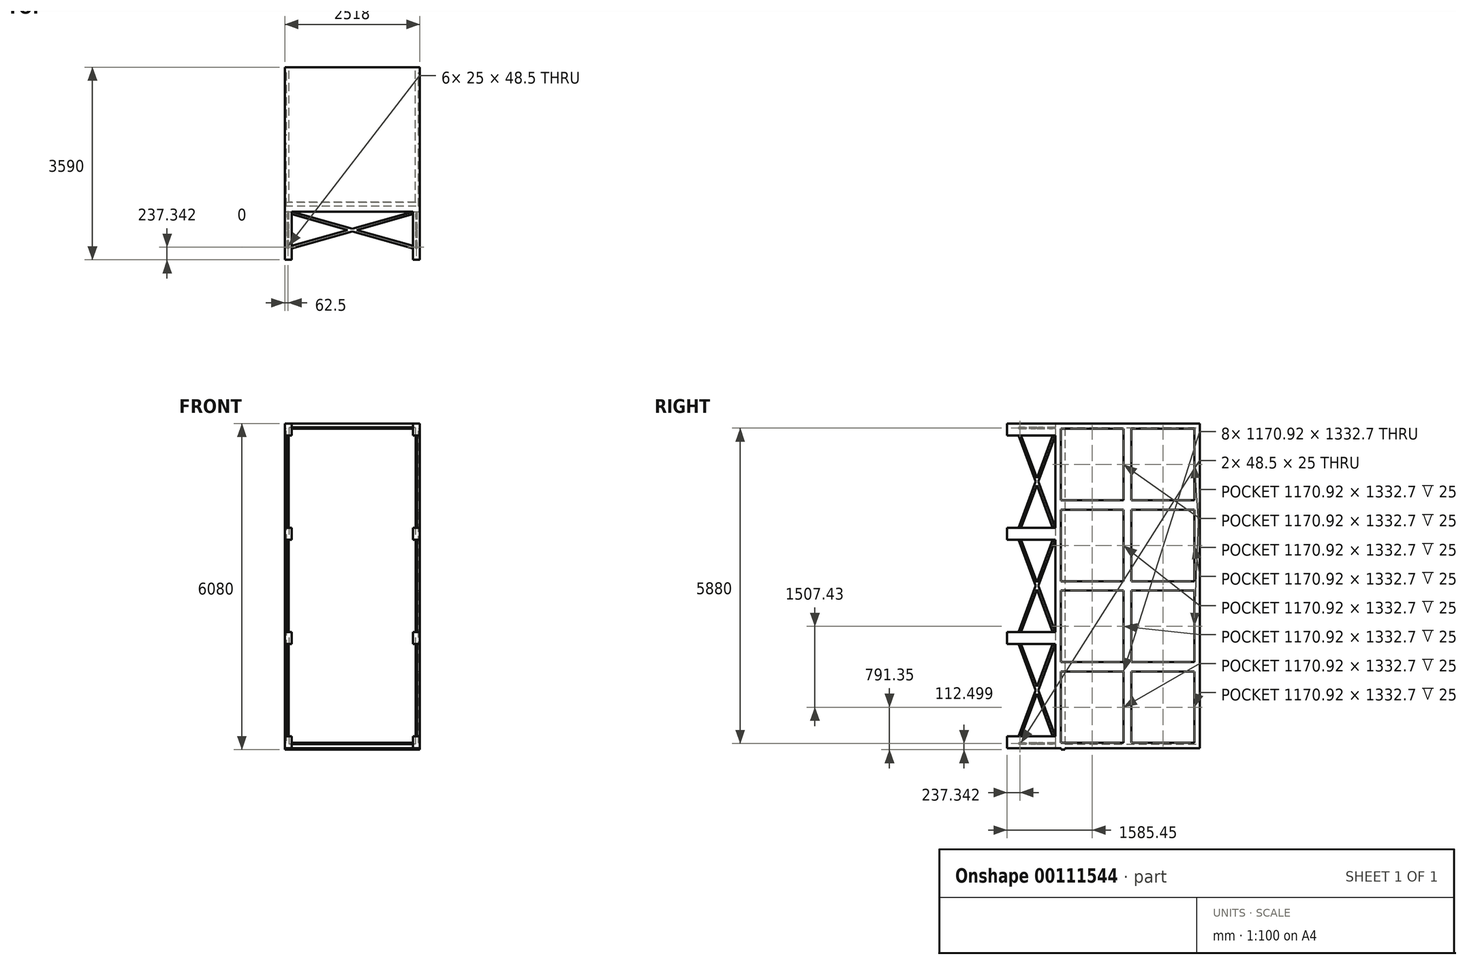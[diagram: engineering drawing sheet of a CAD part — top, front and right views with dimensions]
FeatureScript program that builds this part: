
annotation { "Feature Type Name" : "Feature", "Feature Type Description" : "" }
export const myFeature = defineFeature(function(context is Context, id is Id, definition is map)
    precondition{}
    {
        {
            var Q0;
            Q0=qCreatedBy(makeId("Right.planeOp"),FACE);
            var sketch = newSketch(context, id + "F0", { "sketchPlane" : qUnion([Q0])});
            skLineSegment(sketch, "E0.bottom", {"start": v(4722.94, 3226.74) * mm, "end": v(8312.94, 3226.74) * mm});
            skLineSegment(sketch, "E0.top", {"start": v(4722.94, -2828.26) * mm, "end": v(8312.94, -2828.26) * mm});
            skLineSegment(sketch, "E0.left", {"start": v(4722.94, 3226.74) * mm, "end": v(4722.94, -2828.26) * mm});
            skLineSegment(sketch, "E0.right", {"start": v(8312.94, 3226.74) * mm, "end": v(8312.94, -2828.26) * mm});
            skSolve(sketch);
        }
        {
            var Q0;
            Q0=qSketchRegion(id+"F0",true);
            extrude(context, id + "F1", {"entities" : qUnion([Q0]), "depth" : 2518 * mm});
        }
        {
            var Q0;
            Q0=makeQuery(id+"F1.opExtrude","SWEPT_FACE",FACE,{"disambiguationData":[OSD([sQuery(id+"F0.wireOp",EDGE,"E0.top")])]});
            var sketch = newSketch(context, id + "F2", { "sketchPlane" : qUnion([Q0])});
            skLineSegment(sketch, "E1.bottom", {"start": v(0, -5728.24) * mm, "end": v(2518, -5728.24) * mm});
            skLineSegment(sketch, "E1.top", {"start": v(0, -5798.24) * mm, "end": v(2518, -5798.24) * mm});
            skLineSegment(sketch, "E1.left", {"start": v(0, -5728.24) * mm, "end": v(0, -5798.24) * mm});
            skLineSegment(sketch, "E1.right", {"start": v(2518, -5728.24) * mm, "end": v(2518, -5798.24) * mm});
            skSolve(sketch);
        }
        {
            var Q0;
            Q0=qSketchRegion(id+"F2",true);
            extrude(context, id + "F3", {"entities" : qUnion([Q0]), "operationType" : NewBodyOperationType.ADD, "depth" : 25 * mm});
        }
        {
            var Q0;
            Q0=makeQuery(id+"F1.opExtrude","SWEPT_FACE",FACE,{"disambiguationData":[OSD([sQuery(id+"F0.wireOp",EDGE,"E0.right")])]});
            var sketch = newSketch(context, id + "F4", { "sketchPlane" : qUnion([Q0])});
            skLineSegment(sketch, "E2.0", {"start": v(-2438, 3146.74) * mm, "end": v(-80, 3146.74) * mm});
            skLineSegment(sketch, "E2.1", {"start": v(-2438, 3146.74) * mm, "end": v(-2438, -2748.26) * mm});
            skLineSegment(sketch, "E2.2", {"start": v(-2438, -2748.26) * mm, "end": v(-80, -2748.26) * mm});
            skLineSegment(sketch, "E2.3", {"start": v(-80, 3146.74) * mm, "end": v(-80, -2748.26) * mm});
            skSolve(sketch);
        }
        {
            var Q0;
            Q0=qSketchRegion(id+"F4",true);
            var Q1;
            Q1=makeQuery(id+"F3.opExtrude","SWEPT_FACE",FACE,{"disambiguationData":[OSD([sQuery(id+"F2.wireOp",EDGE,"E1.top")])]});
            extrude(context, id + "F5", {"entities" : qUnion([Q0]), "operationType" : NewBodyOperationType.REMOVE, "endBound" : BoundingType.UP_TO_SURFACE, "oppositeDirection" : true, "endBoundEntityFace" : qUnion([Q1]), "depth" : 25 * mm});
        }
        {
            var Q0;
            Q0=makeQuery(id+"F1.opExtrude","SWEPT_FACE",FACE,{"disambiguationData":[OSD([sQuery(id+"F0.wireOp",EDGE,"E0.left")])]});
            var sketch = newSketch(context, id + "F6", { "sketchPlane" : qUnion([Q0])});
            skLineSegment(sketch, "E3.bottom", {"start": v(0, 3226.74) * mm, "end": v(127, 3226.74) * mm});
            skLineSegment(sketch, "E3.top", {"start": v(0, 3005.36) * mm, "end": v(127, 3005.36) * mm});
            skLineSegment(sketch, "E3.left", {"start": v(0, 3226.74) * mm, "end": v(0, 3005.36) * mm});
            skLineSegment(sketch, "E3.right", {"start": v(127, 3226.74) * mm, "end": v(127, 3005.36) * mm});
            skLineSegment(sketch, "E4.0.1.0", {"start": v(0, 1282.2) * mm, "end": v(127, 1282.2) * mm});
            skLineSegment(sketch, "E4.0.1.1", {"start": v(0, 1282.2) * mm, "end": v(0, 1060.82) * mm});
            skLineSegment(sketch, "E4.0.1.2", {"start": v(127, 1282.2) * mm, "end": v(127, 1060.82) * mm});
            skLineSegment(sketch, "E4.0.1.3", {"start": v(0, 1060.82) * mm, "end": v(127, 1060.82) * mm});
            skLineSegment(sketch, "E4.0.2.0", {"start": v(0, -662.34) * mm, "end": v(127, -662.34) * mm});
            skLineSegment(sketch, "E4.0.2.1", {"start": v(0, -662.34) * mm, "end": v(0, -883.72) * mm});
            skLineSegment(sketch, "E4.0.2.2", {"start": v(127, -662.34) * mm, "end": v(127, -883.72) * mm});
            skLineSegment(sketch, "E4.0.2.3", {"start": v(0, -883.72) * mm, "end": v(127, -883.72) * mm});
            skLineSegment(sketch, "E4.0.3.0", {"start": v(0, -2606.89) * mm, "end": v(127, -2606.89) * mm});
            skLineSegment(sketch, "E4.0.3.1", {"start": v(0, -2606.89) * mm, "end": v(0, -2828.26) * mm});
            skLineSegment(sketch, "E4.0.3.2", {"start": v(127, -2606.89) * mm, "end": v(127, -2828.26) * mm});
            skLineSegment(sketch, "E4.0.3.3", {"start": v(0, -2828.26) * mm, "end": v(127, -2828.26) * mm});
            skLineSegment(sketch, "E4.1.0.0", {"start": v(2391, 3226.74) * mm, "end": v(2518, 3226.74) * mm});
            skLineSegment(sketch, "E4.1.0.1", {"start": v(2391, 3226.74) * mm, "end": v(2391, 3005.36) * mm});
            skLineSegment(sketch, "E4.1.0.2", {"start": v(2518, 3226.74) * mm, "end": v(2518, 3005.36) * mm});
            skLineSegment(sketch, "E4.1.0.3", {"start": v(2391, 3005.36) * mm, "end": v(2518, 3005.36) * mm});
            skLineSegment(sketch, "E4.1.1.0", {"start": v(2391, 1282.2) * mm, "end": v(2518, 1282.2) * mm});
            skLineSegment(sketch, "E4.1.1.1", {"start": v(2391, 1282.2) * mm, "end": v(2391, 1060.82) * mm});
            skLineSegment(sketch, "E4.1.1.2", {"start": v(2518, 1282.2) * mm, "end": v(2518, 1060.82) * mm});
            skLineSegment(sketch, "E4.1.1.3", {"start": v(2391, 1060.82) * mm, "end": v(2518, 1060.82) * mm});
            skLineSegment(sketch, "E4.1.2.0", {"start": v(2391, -662.34) * mm, "end": v(2518, -662.34) * mm});
            skLineSegment(sketch, "E4.1.2.1", {"start": v(2391, -662.34) * mm, "end": v(2391, -883.72) * mm});
            skLineSegment(sketch, "E4.1.2.2", {"start": v(2518, -662.34) * mm, "end": v(2518, -883.72) * mm});
            skLineSegment(sketch, "E4.1.2.3", {"start": v(2391, -883.72) * mm, "end": v(2518, -883.72) * mm});
            skLineSegment(sketch, "E4.1.3.0", {"start": v(2391, -2606.89) * mm, "end": v(2518, -2606.89) * mm});
            skLineSegment(sketch, "E4.1.3.1", {"start": v(2391, -2606.89) * mm, "end": v(2391, -2828.26) * mm});
            skLineSegment(sketch, "E4.1.3.2", {"start": v(2518, -2606.89) * mm, "end": v(2518, -2828.26) * mm});
            skLineSegment(sketch, "E4.1.3.3", {"start": v(2391, -2828.26) * mm, "end": v(2518, -2828.26) * mm});
            skLineSegment(sketch, "E4.direction1", {"start": v(0, 3226.74) * mm, "end": v(2391, 3226.74) * mm, "construction": true});
            skLineSegment(sketch, "E4.direction2", {"start": v(0, 3226.74) * mm, "end": v(0, 1282.2) * mm, "construction": true});
            skLineSegment(sketch, "E5.2", {"start": v(2518, 3226.74) * mm, "end": v(2518, -2828.26) * mm});
            skLineSegment(sketch, "E5.3", {"start": v(0, 3226.74) * mm, "end": v(0, -2828.26) * mm});
            skLineSegment(sketch, "E5.4", {"start": v(2518, -2828.26) * mm, "end": v(0, -2828.26) * mm});
            skSolve(sketch);
        }
        {
            var Q0;
            {var subQ15=sQuery(id+"F6.wireOp",EDGE,"E3.top");Q0=makeQuery(id+"F6.imprint","IMPRINT",FACE,{"disambiguationData":[TD([[makeQuery(id+"F6.imprint","IMPRINT",EDGE,{"derivedFrom":subQ15}),-1.0]])]});}
            extrude(context, id + "F7", {"entities" : qUnion([Q0]), "operationType" : NewBodyOperationType.REMOVE, "oppositeDirection" : true, "depth" : 900 * mm});
        }
        {
            var Q0;
            Q0=makeQuery(id+"F3.boolean.opBoolean","MERGE",FACE,{"derivedFrom":[makeQuery(id+"F1.opExtrude","CAP_FACE",FACE,{"disambiguationData":[OSD([sQuery(id+"F0.wireOp",EDGE,"E0.bottom"),sQuery(id+"F0.wireOp",EDGE,"E0.top"),sQuery(id+"F0.wireOp",EDGE,"E0.left"),sQuery(id+"F0.wireOp",EDGE,"E0.right")])],"isStart":true}),makeQuery(id+"F3.opExtrude","SWEPT_FACE",FACE,{"disambiguationData":[OSD([sQuery(id+"F2.wireOp",EDGE,"E1.left")])]})]});
            var sketch = newSketch(context, id + "F8", { "sketchPlane" : qUnion([Q0])});
            skLineSegment(sketch, "E6", {"start": v(-5622.94, -2606.89) * mm, "end": v(-5303.73, -1745.3) * mm});
            skLineSegment(sketch, "E7", {"start": v(-4984.53, -883.72) * mm, "end": v(-4936.03, -883.72) * mm});
            skLineSegment(sketch, "E8", {"start": v(-4936.03, -883.72) * mm, "end": v(-5255.24, -1745.3) * mm});
            skLineSegment(sketch, "E9", {"start": v(-5622.94, -1745.3) * mm, "end": v(-4658.41, -1745.3) * mm, "construction": true});
            skLineSegment(sketch, "E10.MirrorCS", {"start": v(-5622.94, -883.72) * mm, "end": v(-5303.73, -1745.3) * mm});
            skLineSegment(sketch, "E11.MirrorCS", {"start": v(-4936.03, -2606.89) * mm, "end": v(-5255.24, -1745.3) * mm});
            skLineSegment(sketch, "E12.0.1.0", {"start": v(-5622.94, -662.34) * mm, "end": v(-4984.53, 1060.82) * mm});
            skLineSegment(sketch, "E12.0.1.1", {"start": v(-4936.03, 1060.82) * mm, "end": v(-5574.44, -662.34) * mm});
            skLineSegment(sketch, "E12.0.1.2", {"start": v(-5622.94, 1060.82) * mm, "end": v(-4984.53, -662.34) * mm});
            skLineSegment(sketch, "E12.0.1.3", {"start": v(-4936.03, -662.34) * mm, "end": v(-5574.44, 1060.82) * mm});
            skLineSegment(sketch, "E12.0.2.0", {"start": v(-5622.94, 1282.2) * mm, "end": v(-4984.53, 3005.36) * mm});
            skLineSegment(sketch, "E12.0.2.1", {"start": v(-4936.03, 3005.36) * mm, "end": v(-5574.44, 1282.2) * mm});
            skLineSegment(sketch, "E12.0.2.2", {"start": v(-5622.94, 3005.36) * mm, "end": v(-4984.53, 1282.2) * mm});
            skLineSegment(sketch, "E12.0.2.3", {"start": v(-4936.03, 1282.2) * mm, "end": v(-5574.44, 3005.36) * mm});
            skLineSegment(sketch, "E12.direction1", {"start": v(-5622.94, -2606.89) * mm, "end": v(-5597.94, -2606.89) * mm, "construction": true});
            skLineSegment(sketch, "E12.direction2", {"start": v(-5622.94, -2606.89) * mm, "end": v(-5622.94, -662.34) * mm, "construction": true});
            skLineSegment(sketch, "E13.trimOffspring", {"start": v(-5279.48, -1810.75) * mm, "end": v(-5574.44, -2606.89) * mm});
            skLineSegment(sketch, "E14.trimOffspring", {"start": v(-5279.48, -1810.75) * mm, "end": v(-4984.53, -2606.89) * mm});
            skLineSegment(sketch, "E15.trimOffspring", {"start": v(-5279.48, -1679.85) * mm, "end": v(-4984.53, -883.72) * mm});
            skLineSegment(sketch, "E16.trimOffspring", {"start": v(-5279.48, -1679.85) * mm, "end": v(-5574.44, -883.72) * mm});
            skSolve(sketch);
        }
        {
            var Q0;
            Q0=qSketchRegion(id+"F8",true);
            var Q1;
            {var subQ5=sQuery(id+"F8.wireOp",EDGE,"E12.0.1.0");var subQ7=sQuery(id+"F8.wireOp",EDGE,"E12.0.1.2");var subQ9=makeQuery(id+"F8.imprint","INTERSECT",VERTEX,{"derivedFrom":[subQ5,subQ7]});Q1=makeQuery(id+"F8.imprint","IMPRINT",FACE,{"disambiguationData":[TD([[makeQuery(id+"F8.imprint","IMPRINT",EDGE,{"disambiguationData":[TD([[subQ9,-1.0]])],"derivedFrom":subQ7}),-1.0]])]});}
            var Q2;
            {var subQ1=sQuery(id+"F8.wireOp",EDGE,"E12.0.1.3");var subQ5=sQuery(id+"F8.wireOp",EDGE,"E12.0.1.1");var subQ6=makeQuery(id+"F8.imprint","INTERSECT",VERTEX,{"derivedFrom":[subQ5,subQ1]});Q2=makeQuery(id+"F8.imprint","IMPRINT",FACE,{"disambiguationData":[TD([[makeQuery(id+"F8.imprint","IMPRINT",EDGE,{"disambiguationData":[TD([[subQ6,-1.0]])],"derivedFrom":subQ5}),1.0]])]});}
            var Q3;
            {var subQ5=sQuery(id+"F8.wireOp",EDGE,"E12.0.1.2");var subQ7=sQuery(id+"F8.wireOp",EDGE,"E12.0.1.0");var subQ8=makeQuery(id+"F8.imprint","INTERSECT",VERTEX,{"derivedFrom":[subQ7,subQ5]});Q3=makeQuery(id+"F8.imprint","IMPRINT",FACE,{"disambiguationData":[TD([[makeQuery(id+"F8.imprint","IMPRINT",EDGE,{"disambiguationData":[TD([[subQ8,-1.0]])],"derivedFrom":subQ7}),1.0]])]});}
            var Q4;
            {var subQ1=sQuery(id+"F8.wireOp",EDGE,"E12.0.1.1");var subQ5=sQuery(id+"F8.wireOp",EDGE,"E12.0.1.3");var subQ6=makeQuery(id+"F8.imprint","INTERSECT",VERTEX,{"derivedFrom":[subQ1,subQ5]});Q4=makeQuery(id+"F8.imprint","IMPRINT",FACE,{"disambiguationData":[TD([[makeQuery(id+"F8.imprint","IMPRINT",EDGE,{"disambiguationData":[TD([[subQ6,-1.0]])],"derivedFrom":subQ5}),-1.0]])]});}
            var Q5;
            {var subQ5=sQuery(id+"F8.wireOp",EDGE,"E12.0.2.0");var subQ7=sQuery(id+"F8.wireOp",EDGE,"E12.0.2.2");var subQ9=makeQuery(id+"F8.imprint","INTERSECT",VERTEX,{"derivedFrom":[subQ5,subQ7]});Q5=makeQuery(id+"F8.imprint","IMPRINT",FACE,{"disambiguationData":[TD([[makeQuery(id+"F8.imprint","IMPRINT",EDGE,{"disambiguationData":[TD([[subQ9,-1.0]])],"derivedFrom":subQ7}),-1.0]])]});}
            var Q6;
            {var subQ5=sQuery(id+"F8.wireOp",EDGE,"E12.0.2.2");var subQ7=sQuery(id+"F8.wireOp",EDGE,"E12.0.2.0");var subQ9=makeQuery(id+"F8.imprint","INTERSECT",VERTEX,{"derivedFrom":[subQ7,subQ5]});Q6=makeQuery(id+"F8.imprint","IMPRINT",FACE,{"disambiguationData":[TD([[makeQuery(id+"F8.imprint","IMPRINT",EDGE,{"disambiguationData":[TD([[subQ9,-1.0]])],"derivedFrom":subQ7}),1.0]])]});}
            var Q7;
            {var subQ1=sQuery(id+"F8.wireOp",EDGE,"E12.0.2.1");var subQ5=sQuery(id+"F8.wireOp",EDGE,"E12.0.2.3");var subQ6=makeQuery(id+"F8.imprint","INTERSECT",VERTEX,{"derivedFrom":[subQ1,subQ5]});Q7=makeQuery(id+"F8.imprint","IMPRINT",FACE,{"disambiguationData":[TD([[makeQuery(id+"F8.imprint","IMPRINT",EDGE,{"disambiguationData":[TD([[subQ6,-1.0]])],"derivedFrom":subQ5}),-1.0]])]});}
            var Q8;
            {var subQ0=sQuery(id+"F8.wireOp",EDGE,"E12.0.2.3");var subQ1=sQuery(id+"F8.wireOp",EDGE,"E12.0.2.1");var subQ2=makeQuery(id+"F8.imprint","INTERSECT",VERTEX,{"derivedFrom":[subQ1,subQ0]});Q8=makeQuery(id+"F8.imprint","IMPRINT",FACE,{"disambiguationData":[TD([[makeQuery(id+"F8.imprint","IMPRINT",EDGE,{"disambiguationData":[TD([[subQ2,-1.0]])],"derivedFrom":subQ1}),1.0]])]});}
            var Q9;
            {var subQ8=sQuery(id+"F8.wireOp",EDGE,"E6");Q9=makeQuery(id+"F8.imprint","IMPRINT",FACE,{"disambiguationData":[TD([[makeQuery(id+"F8.imprint","IMPRINT",EDGE,{"derivedFrom":subQ8}),-1.0]])]});}
            extrude(context, id + "F9", {"entities" : qUnion([Q0, Q1, Q2, Q3, Q4, Q5, Q6, Q7, Q8, Q9]), "operationType" : NewBodyOperationType.ADD, "oppositeDirection" : true, "depth" : 75 * mm, "hasSecondDirection" : true, "secondDirectionOppositeDirection" : true, "secondDirectionDepth" : 50 * mm});
        }
        {
            var Q0;
            Q0=makeQuery(id+"F3.boolean.opBoolean","MERGE",FACE,{"derivedFrom":[makeQuery(id+"F1.opExtrude","CAP_FACE",FACE,{"disambiguationData":[OSD([sQuery(id+"F0.wireOp",EDGE,"E0.bottom"),sQuery(id+"F0.wireOp",EDGE,"E0.top"),sQuery(id+"F0.wireOp",EDGE,"E0.left"),sQuery(id+"F0.wireOp",EDGE,"E0.right")])],"isStart":false}),makeQuery(id+"F3.opExtrude","SWEPT_FACE",FACE,{"disambiguationData":[OSD([sQuery(id+"F2.wireOp",EDGE,"E1.right")])]})]});
            var sketch = newSketch(context, id + "F10", { "sketchPlane" : qUnion([Q0])});
            skLineSegment(sketch, "E17.0", {"start": v(5279.48, 2209.23) * mm, "end": v(4984.53, 3005.36) * mm});
            skLineSegment(sketch, "E17.1", {"start": v(5279.48, 2209.23) * mm, "end": v(5574.44, 3005.36) * mm});
            skLineSegment(sketch, "E17.2", {"start": v(5622.94, 3005.36) * mm, "end": v(5303.73, 2143.78) * mm});
            skLineSegment(sketch, "E17.3", {"start": v(5622.94, 1282.2) * mm, "end": v(5303.73, 2143.78) * mm});
            skLineSegment(sketch, "E17.4", {"start": v(5279.48, 2078.33) * mm, "end": v(5574.44, 1282.2) * mm});
            skLineSegment(sketch, "E17.5", {"start": v(5279.48, 2078.33) * mm, "end": v(4984.53, 1282.2) * mm});
            skLineSegment(sketch, "E17.6", {"start": v(4936.03, 1282.2) * mm, "end": v(5255.24, 2143.78) * mm});
            skLineSegment(sketch, "E17.7", {"start": v(4936.03, 3005.36) * mm, "end": v(5255.24, 2143.78) * mm});
            skLineSegment(sketch, "E18.0", {"start": v(4936.03, 1060.82) * mm, "end": v(5255.24, 199.24) * mm});
            skLineSegment(sketch, "E18.1", {"start": v(5279.48, 264.69) * mm, "end": v(4984.53, 1060.82) * mm});
            skLineSegment(sketch, "E18.2", {"start": v(5279.48, 264.69) * mm, "end": v(5574.44, 1060.82) * mm});
            skLineSegment(sketch, "E18.3", {"start": v(5622.94, 1060.82) * mm, "end": v(5303.73, 199.24) * mm});
            skLineSegment(sketch, "E18.4", {"start": v(5622.94, -662.34) * mm, "end": v(5303.73, 199.24) * mm});
            skLineSegment(sketch, "E18.5", {"start": v(5279.48, 133.79) * mm, "end": v(5574.44, -662.34) * mm});
            skLineSegment(sketch, "E18.6", {"start": v(4936.03, -662.34) * mm, "end": v(5255.24, 199.24) * mm});
            skLineSegment(sketch, "E18.7", {"start": v(5279.48, 133.79) * mm, "end": v(4984.53, -662.34) * mm});
            skLineSegment(sketch, "E19.0", {"start": v(5279.48, -1679.85) * mm, "end": v(4984.53, -883.72) * mm});
            skLineSegment(sketch, "E19.1", {"start": v(4936.03, -883.72) * mm, "end": v(5255.24, -1745.3) * mm});
            skLineSegment(sketch, "E19.2", {"start": v(5279.48, -1679.85) * mm, "end": v(5574.44, -883.72) * mm});
            skLineSegment(sketch, "E19.3", {"start": v(5622.94, -883.72) * mm, "end": v(5303.73, -1745.3) * mm});
            skLineSegment(sketch, "E19.4", {"start": v(5622.94, -2606.89) * mm, "end": v(5303.73, -1745.3) * mm});
            skLineSegment(sketch, "E19.5", {"start": v(5279.48, -1810.75) * mm, "end": v(5574.44, -2606.89) * mm});
            skLineSegment(sketch, "E19.6", {"start": v(5279.48, -1810.75) * mm, "end": v(4984.53, -2606.89) * mm});
            skLineSegment(sketch, "E19.7", {"start": v(4936.03, -2606.89) * mm, "end": v(5255.24, -1745.3) * mm});
            skLineSegment(sketch, "E20.0", {"start": v(5622.94, 3005.36) * mm, "end": v(4722.94, 3005.36) * mm});
            skLineSegment(sketch, "E20.1", {"start": v(5622.94, 1282.2) * mm, "end": v(4722.94, 1282.2) * mm});
            skLineSegment(sketch, "E20.2", {"start": v(5622.94, 1060.82) * mm, "end": v(4722.94, 1060.82) * mm});
            skLineSegment(sketch, "E20.3", {"start": v(5622.94, -662.34) * mm, "end": v(4722.94, -662.34) * mm});
            skLineSegment(sketch, "E20.4", {"start": v(5622.94, -883.72) * mm, "end": v(4722.94, -883.72) * mm});
            skLineSegment(sketch, "E20.5", {"start": v(5622.94, -2606.89) * mm, "end": v(4722.94, -2606.89) * mm});
            skSolve(sketch);
        }
        {
            var Q0;
            {var subQ10=sQuery(id+"F10.wireOp",EDGE,"E17.0");Q0=makeQuery(id+"F10.imprint","IMPRINT",FACE,{"disambiguationData":[TD([[makeQuery(id+"F10.imprint","IMPRINT",EDGE,{"derivedFrom":subQ10}),1.0]])]});}
            var Q1;
            {var subQ10=sQuery(id+"F10.wireOp",EDGE,"E18.0");Q1=makeQuery(id+"F10.imprint","IMPRINT",FACE,{"disambiguationData":[TD([[makeQuery(id+"F10.imprint","IMPRINT",EDGE,{"derivedFrom":subQ10}),1.0]])]});}
            var Q2;
            {var subQ10=sQuery(id+"F10.wireOp",EDGE,"E19.0");Q2=makeQuery(id+"F10.imprint","IMPRINT",FACE,{"disambiguationData":[TD([[makeQuery(id+"F10.imprint","IMPRINT",EDGE,{"derivedFrom":subQ10}),1.0]])]});}
            extrude(context, id + "F11", {"entities" : qUnion([Q0, Q1, Q2]), "operationType" : NewBodyOperationType.ADD, "oppositeDirection" : true, "depth" : 75 * mm, "hasSecondDirection" : true, "secondDirectionOppositeDirection" : true, "secondDirectionDepth" : 50 * mm});
        }
        {
            var Q0;
            Q0=makeQuery(id+"F1.opExtrude","SWEPT_FACE",FACE,{"disambiguationData":[OSD([sQuery(id+"F0.wireOp",EDGE,"E0.bottom")])]});
            var sketch = newSketch(context, id + "F12", { "sketchPlane" : qUnion([Q0])});
            skPoint(sketch, "E21.0", {"position": v(2468, 4936.03) * mm});
            skPoint(sketch, "E22.0", {"position": v(2468, 4984.53) * mm});
            skLineSegment(sketch, "E23", {"start": v(127, 5622.94) * mm, "end": v(2391, 4984.53) * mm});
            skLineSegment(sketch, "E24", {"start": v(2391, 4936.03) * mm, "end": v(127, 5574.44) * mm});
            skLineSegment(sketch, "E25", {"start": v(1259, 5622.94) * mm, "end": v(1259, 4855.43) * mm, "construction": true});
            skLineSegment(sketch, "E26.MirrorCS", {"start": v(2391, 5622.94) * mm, "end": v(127, 4984.53) * mm});
            skLineSegment(sketch, "E27.MirrorCS", {"start": v(127, 4936.03) * mm, "end": v(2391, 5574.44) * mm});
            skSolve(sketch);
        }
        {
            var Q0;
            Q0=qSketchRegion(id+"F12",true);
            var Q1;
            {var subQ5=sQuery(id+"F12.wireOp",EDGE,"E23");var subQ7=sQuery(id+"F12.wireOp",EDGE,"E26.MirrorCS");var subQ9=makeQuery(id+"F12.imprint","INTERSECT",VERTEX,{"derivedFrom":[subQ5,subQ7]});Q1=makeQuery(id+"F12.imprint","IMPRINT",FACE,{"disambiguationData":[TD([[makeQuery(id+"F12.imprint","IMPRINT",EDGE,{"disambiguationData":[TD([[subQ9,-1.0]])],"derivedFrom":subQ7}),-1.0]])]});}
            var Q2;
            {var subQ5=sQuery(id+"F12.wireOp",EDGE,"E26.MirrorCS");var subQ7=sQuery(id+"F12.wireOp",EDGE,"E23");var subQ9=makeQuery(id+"F12.imprint","INTERSECT",VERTEX,{"derivedFrom":[subQ7,subQ5]});Q2=makeQuery(id+"F12.imprint","IMPRINT",FACE,{"disambiguationData":[TD([[makeQuery(id+"F12.imprint","IMPRINT",EDGE,{"disambiguationData":[TD([[subQ9,-1.0]])],"derivedFrom":subQ7}),1.0]])]});}
            var Q3;
            {var subQ1=sQuery(id+"F12.wireOp",EDGE,"E27.MirrorCS");var subQ5=sQuery(id+"F12.wireOp",EDGE,"E24");var subQ6=makeQuery(id+"F12.imprint","INTERSECT",VERTEX,{"derivedFrom":[subQ5,subQ1]});Q3=makeQuery(id+"F12.imprint","IMPRINT",FACE,{"disambiguationData":[TD([[makeQuery(id+"F12.imprint","IMPRINT",EDGE,{"disambiguationData":[TD([[subQ6,-1.0]])],"derivedFrom":subQ5}),1.0]])]});}
            var Q4;
            {var subQ1=sQuery(id+"F12.wireOp",EDGE,"E24");var subQ5=sQuery(id+"F12.wireOp",EDGE,"E27.MirrorCS");var subQ7=makeQuery(id+"F12.imprint","INTERSECT",VERTEX,{"derivedFrom":[subQ1,subQ5]});Q4=makeQuery(id+"F12.imprint","IMPRINT",FACE,{"disambiguationData":[TD([[makeQuery(id+"F12.imprint","IMPRINT",EDGE,{"disambiguationData":[TD([[subQ7,-1.0]])],"derivedFrom":subQ5}),-1.0]])]});}
            extrude(context, id + "F13", {"entities" : qUnion([Q0, Q1, Q2, Q3, Q4]), "operationType" : NewBodyOperationType.ADD, "oppositeDirection" : true, "depth" : 100 * mm, "hasSecondDirection" : true, "secondDirectionOppositeDirection" : true, "secondDirectionDepth" : 75 * mm});
        }
        {
            var Q0;
            {var subQ0=sQuery(id+"F0.wireOp",EDGE,"E0.top");var subQ3=sQuery(id+"F0.wireOp",EDGE,"E0.right");Q0=makeQuery(id+"F3.boolean.opBoolean","SPLIT",FACE,{"disambiguationData":[TD([makeQuery(id+"F1.opExtrude","SWEPT_FACE",FACE,{"disambiguationData":[OSD([subQ3])]})])],"derivedFrom":makeQuery(id+"F1.opExtrude","SWEPT_FACE",FACE,{"disambiguationData":[OSD([subQ0])]})});}
            var sketch = newSketch(context, id + "F14", { "sketchPlane" : qUnion([Q0])});
            skLineSegment(sketch, "E28.0", {"start": v(127, -5622.94) * mm, "end": v(1259, -5303.73) * mm});
            skLineSegment(sketch, "E28.1", {"start": v(1173, -5279.48) * mm, "end": v(127, -5574.44) * mm});
            skLineSegment(sketch, "E28.2", {"start": v(1173, -5279.48) * mm, "end": v(127, -4984.53) * mm});
            skLineSegment(sketch, "E28.3", {"start": v(127, -4936.03) * mm, "end": v(1259, -5255.24) * mm});
            skLineSegment(sketch, "E28.4", {"start": v(2391, -4936.03) * mm, "end": v(1259, -5255.24) * mm});
            skLineSegment(sketch, "E28.5", {"start": v(1345, -5279.48) * mm, "end": v(2391, -4984.53) * mm});
            skLineSegment(sketch, "E28.6", {"start": v(1345, -5279.48) * mm, "end": v(2391, -5574.44) * mm});
            skLineSegment(sketch, "E28.7", {"start": v(2391, -5622.94) * mm, "end": v(1259, -5303.73) * mm});
            skLineSegment(sketch, "E29.8", {"start": v(127, -5622.94) * mm, "end": v(127, -4722.94) * mm});
            skLineSegment(sketch, "E29.9", {"start": v(2391, -5622.94) * mm, "end": v(2391, -4722.94) * mm});
            skSolve(sketch);
        }
        {
            var Q0;
            {var subQ8=sQuery(id+"F14.wireOp",EDGE,"E28.0");Q0=makeQuery(id+"F14.imprint","IMPRINT",FACE,{"disambiguationData":[TD([[makeQuery(id+"F14.imprint","IMPRINT",EDGE,{"derivedFrom":subQ8}),1.0]])]});}
            extrude(context, id + "F15", {"entities" : qUnion([Q0]), "operationType" : NewBodyOperationType.ADD, "oppositeDirection" : true, "depth" : 100 * mm, "hasSecondDirection" : true, "secondDirectionOppositeDirection" : true, "secondDirectionDepth" : 75 * mm});
        }
        {
            var Q0;
            Q0=makeQuery(id+"F3.boolean.opBoolean","MERGE",FACE,{"derivedFrom":[makeQuery(id+"F1.opExtrude","CAP_FACE",FACE,{"disambiguationData":[OSD([sQuery(id+"F0.wireOp",EDGE,"E0.bottom"),sQuery(id+"F0.wireOp",EDGE,"E0.top"),sQuery(id+"F0.wireOp",EDGE,"E0.left"),sQuery(id+"F0.wireOp",EDGE,"E0.right")])],"isStart":true}),makeQuery(id+"F3.opExtrude","SWEPT_FACE",FACE,{"disambiguationData":[OSD([sQuery(id+"F2.wireOp",EDGE,"E1.left")])]})]});
            var sketch = newSketch(context, id + "F16", { "sketchPlane" : qUnion([Q0])});
            skLineSegment(sketch, "E30.0", {"start": v(-4722.94, 3126.74) * mm, "end": v(-8212.94, 3126.74) * mm});
            skLineSegment(sketch, "E30.1", {"start": v(-8212.94, 3126.74) * mm, "end": v(-8212.94, -2728.26) * mm});
            skLineSegment(sketch, "E30.2", {"start": v(-5798.24, -2728.26) * mm, "end": v(-8212.94, -2728.26) * mm});
            skLineSegment(sketch, "E31.bottom", {"start": v(-8212.94, -2728.26) * mm, "end": v(-7042.02, -2728.26) * mm});
            skLineSegment(sketch, "E31.top", {"start": v(-8212.94, -1395.56) * mm, "end": v(-7042.02, -1395.56) * mm});
            skLineSegment(sketch, "E31.left", {"start": v(-8212.94, -2728.26) * mm, "end": v(-8212.94, -1395.56) * mm});
            skLineSegment(sketch, "E31.right", {"start": v(-7042.02, -2728.26) * mm, "end": v(-7042.02, -1395.56) * mm});
            skLineSegment(sketch, "E32.0.1.0", {"start": v(-8212.94, 111.87) * mm, "end": v(-7042.02, 111.87) * mm});
            skLineSegment(sketch, "E32.0.1.1", {"start": v(-7042.02, -1220.83) * mm, "end": v(-7042.02, 111.87) * mm});
            skLineSegment(sketch, "E32.0.1.2", {"start": v(-8212.94, -1220.83) * mm, "end": v(-7042.02, -1220.83) * mm});
            skLineSegment(sketch, "E32.0.1.3", {"start": v(-8212.94, -1220.83) * mm, "end": v(-8212.94, 111.87) * mm});
            skLineSegment(sketch, "E32.0.2.0", {"start": v(-8212.94, 1619.3) * mm, "end": v(-7042.02, 1619.3) * mm});
            skLineSegment(sketch, "E32.0.2.1", {"start": v(-7042.02, 286.6) * mm, "end": v(-7042.02, 1619.3) * mm});
            skLineSegment(sketch, "E32.0.2.2", {"start": v(-8212.94, 286.6) * mm, "end": v(-7042.02, 286.6) * mm});
            skLineSegment(sketch, "E32.0.2.3", {"start": v(-8212.94, 286.6) * mm, "end": v(-8212.94, 1619.3) * mm});
            skLineSegment(sketch, "E32.0.3.0", {"start": v(-8212.94, 3126.74) * mm, "end": v(-7042.02, 3126.74) * mm});
            skLineSegment(sketch, "E32.0.3.1", {"start": v(-7042.02, 1794.04) * mm, "end": v(-7042.02, 3126.74) * mm});
            skLineSegment(sketch, "E32.0.3.2", {"start": v(-8212.94, 1794.04) * mm, "end": v(-7042.02, 1794.04) * mm});
            skLineSegment(sketch, "E32.0.3.3", {"start": v(-8212.94, 1794.04) * mm, "end": v(-8212.94, 3126.74) * mm});
            skLineSegment(sketch, "E32.1.0.0", {"start": v(-6893.85, -1395.56) * mm, "end": v(-5722.94, -1395.56) * mm});
            skLineSegment(sketch, "E32.1.0.1", {"start": v(-5722.94, -2728.26) * mm, "end": v(-5722.94, -1395.56) * mm});
            skLineSegment(sketch, "E32.1.0.2", {"start": v(-6893.85, -2728.26) * mm, "end": v(-5722.94, -2728.26) * mm});
            skLineSegment(sketch, "E32.1.0.3", {"start": v(-6893.85, -2728.26) * mm, "end": v(-6893.85, -1395.56) * mm});
            skLineSegment(sketch, "E32.1.1.0", {"start": v(-6893.85, 111.87) * mm, "end": v(-5722.94, 111.87) * mm});
            skLineSegment(sketch, "E32.1.1.1", {"start": v(-5722.94, -1220.83) * mm, "end": v(-5722.94, 111.87) * mm});
            skLineSegment(sketch, "E32.1.1.2", {"start": v(-6893.85, -1220.83) * mm, "end": v(-5722.94, -1220.83) * mm});
            skLineSegment(sketch, "E32.1.1.3", {"start": v(-6893.85, -1220.83) * mm, "end": v(-6893.85, 111.87) * mm});
            skLineSegment(sketch, "E32.1.2.0", {"start": v(-6893.85, 1619.3) * mm, "end": v(-5722.94, 1619.3) * mm});
            skLineSegment(sketch, "E32.1.2.1", {"start": v(-5722.94, 286.6) * mm, "end": v(-5722.94, 1619.3) * mm});
            skLineSegment(sketch, "E32.1.2.2", {"start": v(-6893.85, 286.6) * mm, "end": v(-5722.94, 286.6) * mm});
            skLineSegment(sketch, "E32.1.2.3", {"start": v(-6893.85, 286.6) * mm, "end": v(-6893.85, 1619.3) * mm});
            skLineSegment(sketch, "E32.1.3.0", {"start": v(-6893.85, 3126.74) * mm, "end": v(-5722.94, 3126.74) * mm});
            skLineSegment(sketch, "E32.1.3.1", {"start": v(-5722.94, 1794.04) * mm, "end": v(-5722.94, 3126.74) * mm});
            skLineSegment(sketch, "E32.1.3.2", {"start": v(-6893.85, 1794.04) * mm, "end": v(-5722.94, 1794.04) * mm});
            skLineSegment(sketch, "E32.1.3.3", {"start": v(-6893.85, 1794.04) * mm, "end": v(-6893.85, 3126.74) * mm});
            skLineSegment(sketch, "E32.direction1", {"start": v(-8212.94, -1395.56) * mm, "end": v(-6893.85, -1395.56) * mm, "construction": true});
            skLineSegment(sketch, "E32.direction2", {"start": v(-8212.94, -1395.56) * mm, "end": v(-8212.94, 111.87) * mm, "construction": true});
            skSolve(sketch);
        }
        {
            var Q0;
            Q0=qSketchRegion(id+"F16",true);
            extrude(context, id + "F17", {"entities" : qUnion([Q0]), "operationType" : NewBodyOperationType.REMOVE, "oppositeDirection" : true, "depth" : 25 * mm});
        }
        {
            var Q0;
            Q0=makeQuery(id+"F3.boolean.opBoolean","MERGE",FACE,{"derivedFrom":[makeQuery(id+"F1.opExtrude","CAP_FACE",FACE,{"disambiguationData":[OSD([sQuery(id+"F0.wireOp",EDGE,"E0.bottom"),sQuery(id+"F0.wireOp",EDGE,"E0.top"),sQuery(id+"F0.wireOp",EDGE,"E0.left"),sQuery(id+"F0.wireOp",EDGE,"E0.right")])],"isStart":false}),makeQuery(id+"F3.opExtrude","SWEPT_FACE",FACE,{"disambiguationData":[OSD([sQuery(id+"F2.wireOp",EDGE,"E1.right")])]})]});
            var sketch = newSketch(context, id + "F18", { "sketchPlane" : qUnion([Q0])});
            skLineSegment(sketch, "E33.0.0", {"start": v(7042.02, 111.87) * mm, "end": v(8212.94, 111.87) * mm});
            skLineSegment(sketch, "E33.0.1", {"start": v(8212.94, 111.87) * mm, "end": v(8212.94, -1220.83) * mm});
            skLineSegment(sketch, "E33.0.2", {"start": v(8212.94, -1220.83) * mm, "end": v(7042.02, -1220.83) * mm});
            skLineSegment(sketch, "E33.0.3", {"start": v(7042.02, -1220.83) * mm, "end": v(7042.02, 111.87) * mm});
            skLineSegment(sketch, "E33.1.0", {"start": v(8212.94, -1395.56) * mm, "end": v(8212.94, -2728.26) * mm});
            skLineSegment(sketch, "E33.1.1", {"start": v(8212.94, -2728.26) * mm, "end": v(7042.02, -2728.26) * mm});
            skLineSegment(sketch, "E33.1.2", {"start": v(7042.02, -2728.26) * mm, "end": v(7042.02, -1395.56) * mm});
            skLineSegment(sketch, "E33.1.3", {"start": v(7042.02, -1395.56) * mm, "end": v(8212.94, -1395.56) * mm});
            skLineSegment(sketch, "E33.2.0", {"start": v(5722.94, -1395.56) * mm, "end": v(6893.85, -1395.56) * mm});
            skLineSegment(sketch, "E33.2.1", {"start": v(6893.85, -1395.56) * mm, "end": v(6893.85, -2728.26) * mm});
            skLineSegment(sketch, "E33.2.2", {"start": v(6893.85, -2728.26) * mm, "end": v(5722.94, -2728.26) * mm});
            skLineSegment(sketch, "E33.2.3", {"start": v(5722.94, -2728.26) * mm, "end": v(5722.94, -1395.56) * mm});
            skLineSegment(sketch, "E33.3.0", {"start": v(5722.94, 111.87) * mm, "end": v(6893.85, 111.87) * mm});
            skLineSegment(sketch, "E33.3.1", {"start": v(6893.85, 111.87) * mm, "end": v(6893.85, -1220.83) * mm});
            skLineSegment(sketch, "E33.3.2", {"start": v(6893.85, -1220.83) * mm, "end": v(5722.94, -1220.83) * mm});
            skLineSegment(sketch, "E33.3.3", {"start": v(5722.94, -1220.83) * mm, "end": v(5722.94, 111.87) * mm});
            skLineSegment(sketch, "E33.4.0", {"start": v(5722.94, 1619.3) * mm, "end": v(6893.85, 1619.3) * mm});
            skLineSegment(sketch, "E33.4.1", {"start": v(6893.85, 1619.3) * mm, "end": v(6893.85, 286.6) * mm});
            skLineSegment(sketch, "E33.4.2", {"start": v(6893.85, 286.6) * mm, "end": v(5722.94, 286.6) * mm});
            skLineSegment(sketch, "E33.4.3", {"start": v(5722.94, 286.6) * mm, "end": v(5722.94, 1619.3) * mm});
            skLineSegment(sketch, "E33.5.0", {"start": v(7042.02, 1619.3) * mm, "end": v(8212.94, 1619.3) * mm});
            skLineSegment(sketch, "E33.5.1", {"start": v(8212.94, 1619.3) * mm, "end": v(8212.94, 286.6) * mm});
            skLineSegment(sketch, "E33.5.2", {"start": v(8212.94, 286.6) * mm, "end": v(7042.02, 286.6) * mm});
            skLineSegment(sketch, "E33.5.3", {"start": v(7042.02, 286.6) * mm, "end": v(7042.02, 1619.3) * mm});
            skLineSegment(sketch, "E33.6.0", {"start": v(7042.02, 3126.74) * mm, "end": v(8212.94, 3126.74) * mm});
            skLineSegment(sketch, "E33.6.1", {"start": v(8212.94, 3126.74) * mm, "end": v(8212.94, 1794.04) * mm});
            skLineSegment(sketch, "E33.6.2", {"start": v(8212.94, 1794.04) * mm, "end": v(7042.02, 1794.04) * mm});
            skLineSegment(sketch, "E33.6.3", {"start": v(7042.02, 1794.04) * mm, "end": v(7042.02, 3126.74) * mm});
            skLineSegment(sketch, "E33.7.0", {"start": v(5722.94, 3126.74) * mm, "end": v(6893.85, 3126.74) * mm});
            skLineSegment(sketch, "E33.7.1", {"start": v(6893.85, 3126.74) * mm, "end": v(6893.85, 1794.04) * mm});
            skLineSegment(sketch, "E33.7.2", {"start": v(6893.85, 1794.04) * mm, "end": v(5722.94, 1794.04) * mm});
            skLineSegment(sketch, "E33.7.3", {"start": v(5722.94, 1794.04) * mm, "end": v(5722.94, 3126.74) * mm});
            skSolve(sketch);
        }
        {
            var Q0;
            Q0=qSketchRegion(id+"F18",true);
            extrude(context, id + "F19", {"entities" : qUnion([Q0]), "operationType" : NewBodyOperationType.REMOVE, "oppositeDirection" : true, "depth" : 25 * mm});
        }
    });
